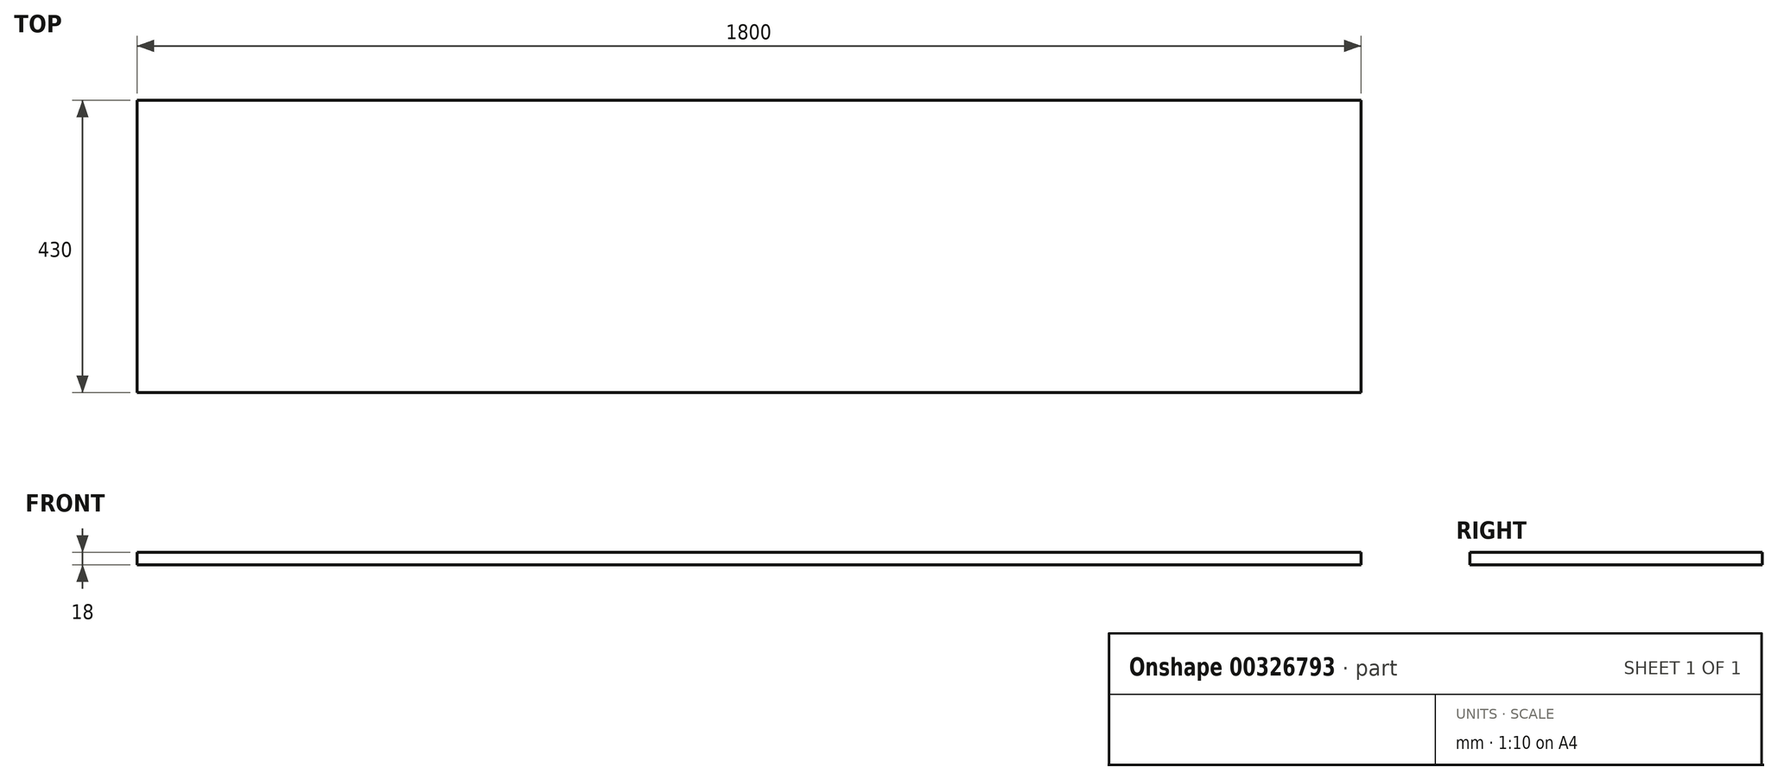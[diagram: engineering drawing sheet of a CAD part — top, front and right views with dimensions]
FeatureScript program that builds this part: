
annotation { "Feature Type Name" : "Feature", "Feature Type Description" : "" }
export const myFeature = defineFeature(function(context is Context, id is Id, definition is map)
    precondition{}
    {
        {
            var Q0;
            Q0=qCreatedBy(makeId("Top.planeOp"),FACE);
            var sketch = newSketch(context, id + "F0", { "sketchPlane" : qUnion([Q0])});
            skLineSegment(sketch, "E0.bottom", {"start": v(0, 0) * mm, "end": v(1800, 0) * mm});
            skLineSegment(sketch, "E0.top", {"start": v(0, 430) * mm, "end": v(1800, 430) * mm});
            skLineSegment(sketch, "E0.left", {"start": v(0, 0) * mm, "end": v(0, 430) * mm});
            skLineSegment(sketch, "E0.right", {"start": v(1800, 0) * mm, "end": v(1800, 430) * mm});
            skSolve(sketch);
        }
        {
            var Q0;
            Q0=qSketchRegion(id+"F0",true);
            extrude(context, id + "F1", {"entities" : qUnion([Q0]), "depth" : 18 * mm});
        }
    });
